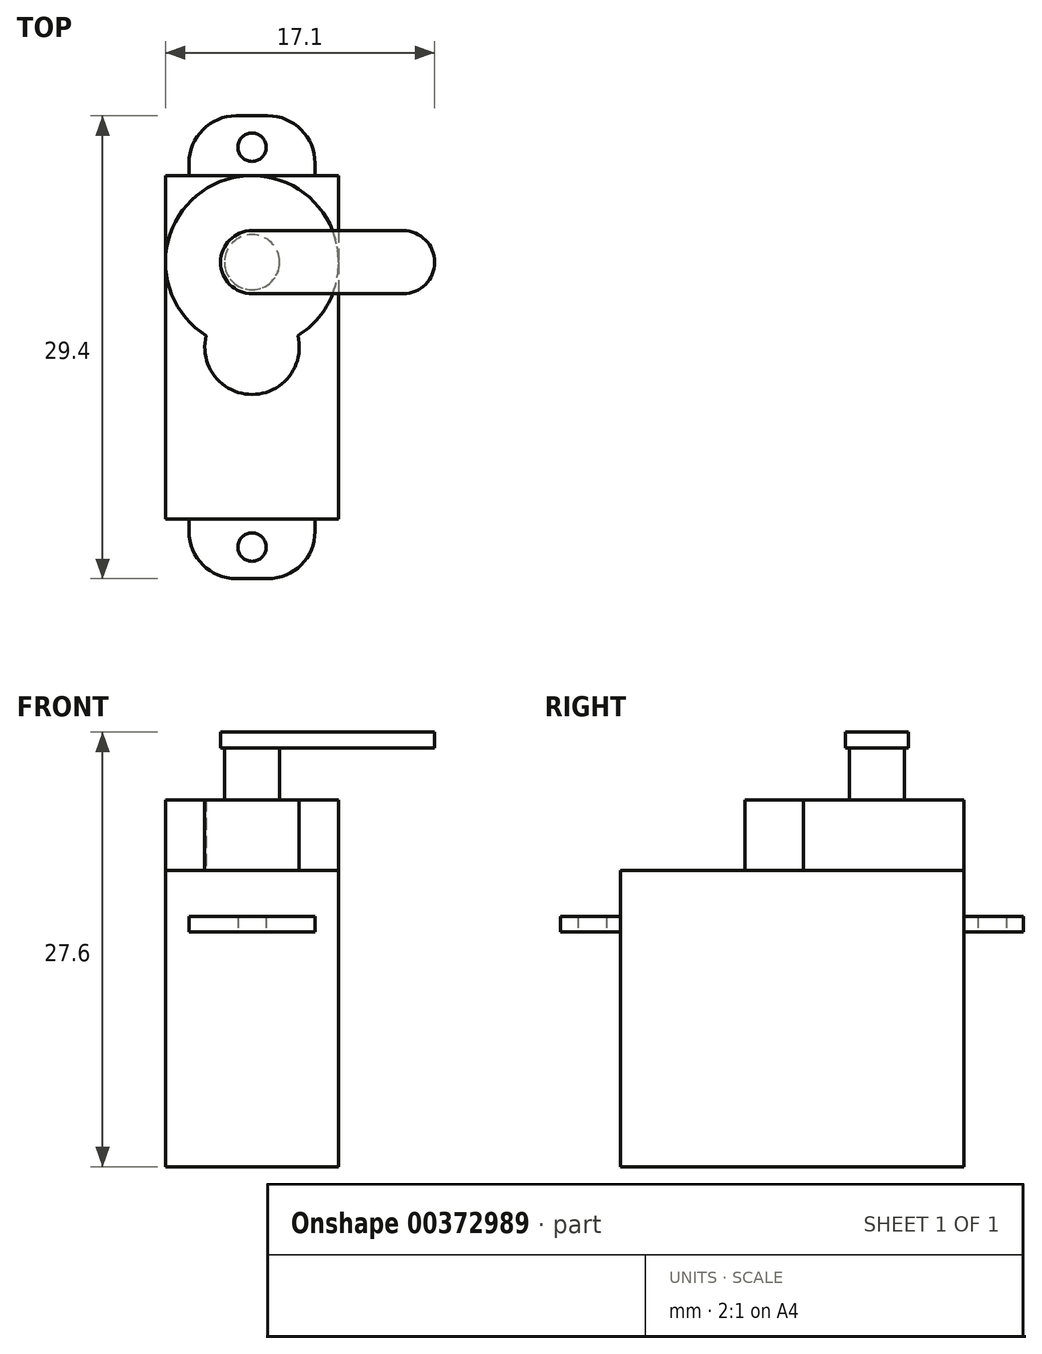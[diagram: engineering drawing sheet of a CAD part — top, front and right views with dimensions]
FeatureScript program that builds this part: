
annotation { "Feature Type Name" : "Feature", "Feature Type Description" : "" }
export const myFeature = defineFeature(function(context is Context, id is Id, definition is map)
    precondition{}
    {
        {
            var Q0;
            Q0=qCreatedBy(makeId("Top.planeOp"),FACE);
            var sketch = newSketch(context, id + "F0", { "sketchPlane" : qUnion([Q0])});
            skLineSegment(sketch, "E0.bottom", {"start": v(-5.5, 10.9) * mm, "end": v(5.5, 10.9) * mm});
            skLineSegment(sketch, "E0.top", {"start": v(-5.5, -10.9) * mm, "end": v(5.5, -10.9) * mm});
            skLineSegment(sketch, "E0.left", {"start": v(-5.5, 10.9) * mm, "end": v(-5.5, -10.9) * mm});
            skLineSegment(sketch, "E0.right", {"start": v(5.5, 10.9) * mm, "end": v(5.5, -10.9) * mm});
            skPoint(sketch, "E0.middle", {"position": v(0, 0) * mm});
            skSolve(sketch);
        }
        {
            var Q0;
            Q0 = qSketchRegion(id + "F0", true);
            extrude(context, id + "F1", {"entities" : qUnion([Q0]), "offsetDistance" : 25 * mm, "depth" : (24 - 5.2) * mm});
        }
        {
            var Q0;
            Q0=qCreatedBy(makeId("Top.planeOp"),FACE);
            cPlane(context, id + "F2", {"entities" : qUnion([Q0]), "cplaneType" : CPlaneType.OFFSET, "offset" : 14.9 * mm, "width" : 150 * mm, "height" : 150 * mm});
        }
        {
            var Q0;
            Q0=qCreatedBy(id+"F2.planeOp",FACE);
            var sketch = newSketch(context, id + "F3", { "sketchPlane" : qUnion([Q0])});
            skLineSegment(sketch, "E1.bottom", {"start": v(4, 10.9) * mm, "end": v(-4, 10.9) * mm});
            skLineSegment(sketch, "E1.top", {"start": v(4, 14.7) * mm, "end": v(-4, 14.7) * mm});
            skLineSegment(sketch, "E1.left", {"start": v(4, 10.9) * mm, "end": v(4, 14.7) * mm});
            skLineSegment(sketch, "E1.right", {"start": v(-4, 10.9) * mm, "end": v(-4, 14.7) * mm});
            skLineSegment(sketch, "E2", {"start": v(0, 0) * mm, "end": v(-14.3, 0) * mm, "construction": true});
            skCircle(sketch, "E3", {"center": v(0, 12.7) * mm, "radius": 0.9 * mm});
            skLineSegment(sketch, "E4.MirrorCS", {"start": v(4, -10.9) * mm, "end": v(-4, -10.9) * mm});
            skLineSegment(sketch, "E5.MirrorCS", {"start": v(4, -10.9) * mm, "end": v(4, -14.7) * mm});
            skCircle(sketch, "E6.MirrorC", {"center": v(0, -12.7) * mm, "radius": 0.9 * mm});
            skLineSegment(sketch, "E7.MirrorCS", {"start": v(4, -14.7) * mm, "end": v(-4, -14.7) * mm});
            skLineSegment(sketch, "E8.MirrorCS", {"start": v(-4, -10.9) * mm, "end": v(-4, -14.7) * mm});
            skLineSegment(sketch, "E9", {"start": v(0, 14.7) * mm, "end": v(0, 0) * mm, "construction": true});
            skSolve(sketch);
        }
        {
            var Q0;
            Q0 = qSketchRegion(id + "F3", true);
            extrude(context, id + "F4", {"entities" : qUnion([Q0]), "operationType" : NewBodyOperationType.ADD, "depth" : 1 * mm, "offsetDistance" : 25 * mm});
        }
        {
            var Q0;
            Q0=makeQuery(id+"F1.opExtrude","CAP_FACE",FACE,{"disambiguationData":[OSD([sQuery(id+"F0.wireOp",EDGE,"E0.bottom"),sQuery(id+"F0.wireOp",EDGE,"E0.top"),sQuery(id+"F0.wireOp",EDGE,"E0.left"),sQuery(id+"F0.wireOp",EDGE,"E0.right")])],"isStart":false});
            var sketch = newSketch(context, id + "F5", { "sketchPlane" : qUnion([Q0])});
            skArc(sketch, "E10", {"start": v(2.9, 0.73) * mm, "mid": v(0, 10.9) * mm, "end": v(-2.9, 0.73) * mm});
            skArc(sketch, "E11", {"start": v(-2.9, 0.73) * mm, "mid": v(0, -3) * mm, "end": v(2.9, 0.73) * mm});
            skSolve(sketch);
        }
        {
            var Q0;
            Q0 = qSketchRegion(id + "F5", true);
            extrude(context, id + "F6", {"entities" : qUnion([Q0]), "operationType" : NewBodyOperationType.ADD, "depth" : 4.5 * mm, "offsetDistance" : 25 * mm});
        }
        {
            var Q0;
            Q0=makeQuery(id+"F6.opExtrude","CAP_FACE",FACE,{"disambiguationData":[OSD([sQuery(id+"F5.wireOp",EDGE,"E10"),sQuery(id+"F5.wireOp",EDGE,"E11")])],"isStart":false});
            var sketch = newSketch(context, id + "F7", { "sketchPlane" : qUnion([Q0])});
            skCircle(sketch, "E12", {"center": v(0, 5.4) * mm, "radius": 1.75 * mm});
            skSolve(sketch);
        }
        {
            var Q0;
            Q0 = qSketchRegion(id + "F7", true);
            extrude(context, id + "F8", {"entities" : qUnion([Q0]), "operationType" : NewBodyOperationType.ADD, "depth" : 3.5 * mm, "offsetDistance" : 25 * mm});
        }
        {
            var Q0;
            Q0=makeQuery(id+"F4.opExtrude","CAP_FACE",FACE,{"disambiguationData":[OSD([sQuery(id+"F3.wireOp",EDGE,"E1.bottom"),sQuery(id+"F3.wireOp",EDGE,"E1.top"),sQuery(id+"F3.wireOp",EDGE,"E1.left"),sQuery(id+"F3.wireOp",EDGE,"E1.right"),sQuery(id+"F3.wireOp",EDGE,"E3")])],"isStart":true});
            cPlane(context, id + "F9", {"entities" : qUnion([Q0]), "cplaneType" : CPlaneType.OFFSET, "offset" : 11.7 * mm, "oppositeDirection" : true, "width" : 150 * mm, "height" : 150 * mm});
        }
        {
            var Q0;
            Q0=qCreatedBy(id+"F9.planeOp",FACE);
            var sketch = newSketch(context, id + "F10", { "sketchPlane" : qUnion([Q0])});
            skLineSegment(sketch, "E13.bottom", {"start": v(-2, -7.4) * mm, "end": v(11.6, -7.4) * mm});
            skLineSegment(sketch, "E13.top", {"start": v(-2, -3.4) * mm, "end": v(11.6, -3.4) * mm});
            skLineSegment(sketch, "E13.left", {"start": v(-2, -7.4) * mm, "end": v(-2, -3.4) * mm});
            skLineSegment(sketch, "E13.right", {"start": v(11.6, -7.4) * mm, "end": v(11.6, -3.4) * mm});
            skLineSegment(sketch, "E14", {"start": v(-2, -5.4) * mm, "end": v(0, -5.4) * mm, "construction": true});
            skLineSegment(sketch, "E15", {"start": v(0, -5.4) * mm, "end": v(0, 0) * mm, "construction": true});
            skSolve(sketch);
        }
        {
            var Q0;
            Q0 = qSketchRegion(id + "F10", true);
            extrude(context, id + "F11", {"entities" : qUnion([Q0]), "operationType" : NewBodyOperationType.ADD, "oppositeDirection" : true, "depth" : 1 * mm, "offsetDistance" : 25 * mm});
        }
        {
            var Q0;
            Q0=makeQuery(id+"F11.opExtrude","SWEPT_EDGE",EDGE,{"disambiguationData":[OSD([sQuery(id+"F10.wireOp",EDGE,"E13.top"),sQuery(id+"F10.wireOp",EDGE,"E13.right")])]});
            var Q1;
            Q1=makeQuery(id+"F11.opExtrude","SWEPT_EDGE",EDGE,{"disambiguationData":[OSD([sQuery(id+"F10.wireOp",EDGE,"E13.bottom"),sQuery(id+"F10.wireOp",EDGE,"E13.right")])]});
            var Q2;
            Q2=makeQuery(id+"F11.opExtrude","SWEPT_EDGE",EDGE,{"disambiguationData":[OSD([sQuery(id+"F10.wireOp",EDGE,"E13.bottom"),sQuery(id+"F10.wireOp",EDGE,"E13.left")])]});
            var Q3;
            Q3=makeQuery(id+"F11.opExtrude","SWEPT_EDGE",EDGE,{"disambiguationData":[OSD([sQuery(id+"F10.wireOp",EDGE,"E13.top"),sQuery(id+"F10.wireOp",EDGE,"E13.left")])]});
            fillet(context, id + "F12", {"entities" : qUnion([Q0, Q1, Q2, Q3]), "tangentPropagation" : true, "radius" : 2 * mm, "defaultsChanged" : false, "vertexSettings" : [], "allowEdgeOverflow" : false});
        }
        {
            var Q0;
            Q0=makeQuery(id+"F4.opExtrude","SWEPT_EDGE",EDGE,{"disambiguationData":[OSD([sQuery(id+"F3.wireOp",EDGE,"E7.MirrorCS"),sQuery(id+"F3.wireOp",EDGE,"E8.MirrorCS")])]});
            var Q1;
            Q1=makeQuery(id+"F4.opExtrude","SWEPT_EDGE",EDGE,{"disambiguationData":[OSD([sQuery(id+"F3.wireOp",EDGE,"E5.MirrorCS"),sQuery(id+"F3.wireOp",EDGE,"E7.MirrorCS")])]});
            var Q2;
            Q2=makeQuery(id+"F4.opExtrude","SWEPT_EDGE",EDGE,{"disambiguationData":[OSD([sQuery(id+"F3.wireOp",EDGE,"E1.top"),sQuery(id+"F3.wireOp",EDGE,"E1.left")])]});
            var Q3;
            Q3=makeQuery(id+"F4.opExtrude","SWEPT_EDGE",EDGE,{"disambiguationData":[OSD([sQuery(id+"F3.wireOp",EDGE,"E1.top"),sQuery(id+"F3.wireOp",EDGE,"E1.right")])]});
            fillet(context, id + "F13", {"entities" : qUnion([Q0, Q1, Q2, Q3]), "tangentPropagation" : true, "radius" : 3 * mm, "defaultsChanged" : false, "vertexSettings" : [], "allowEdgeOverflow" : false});
        }
    });
